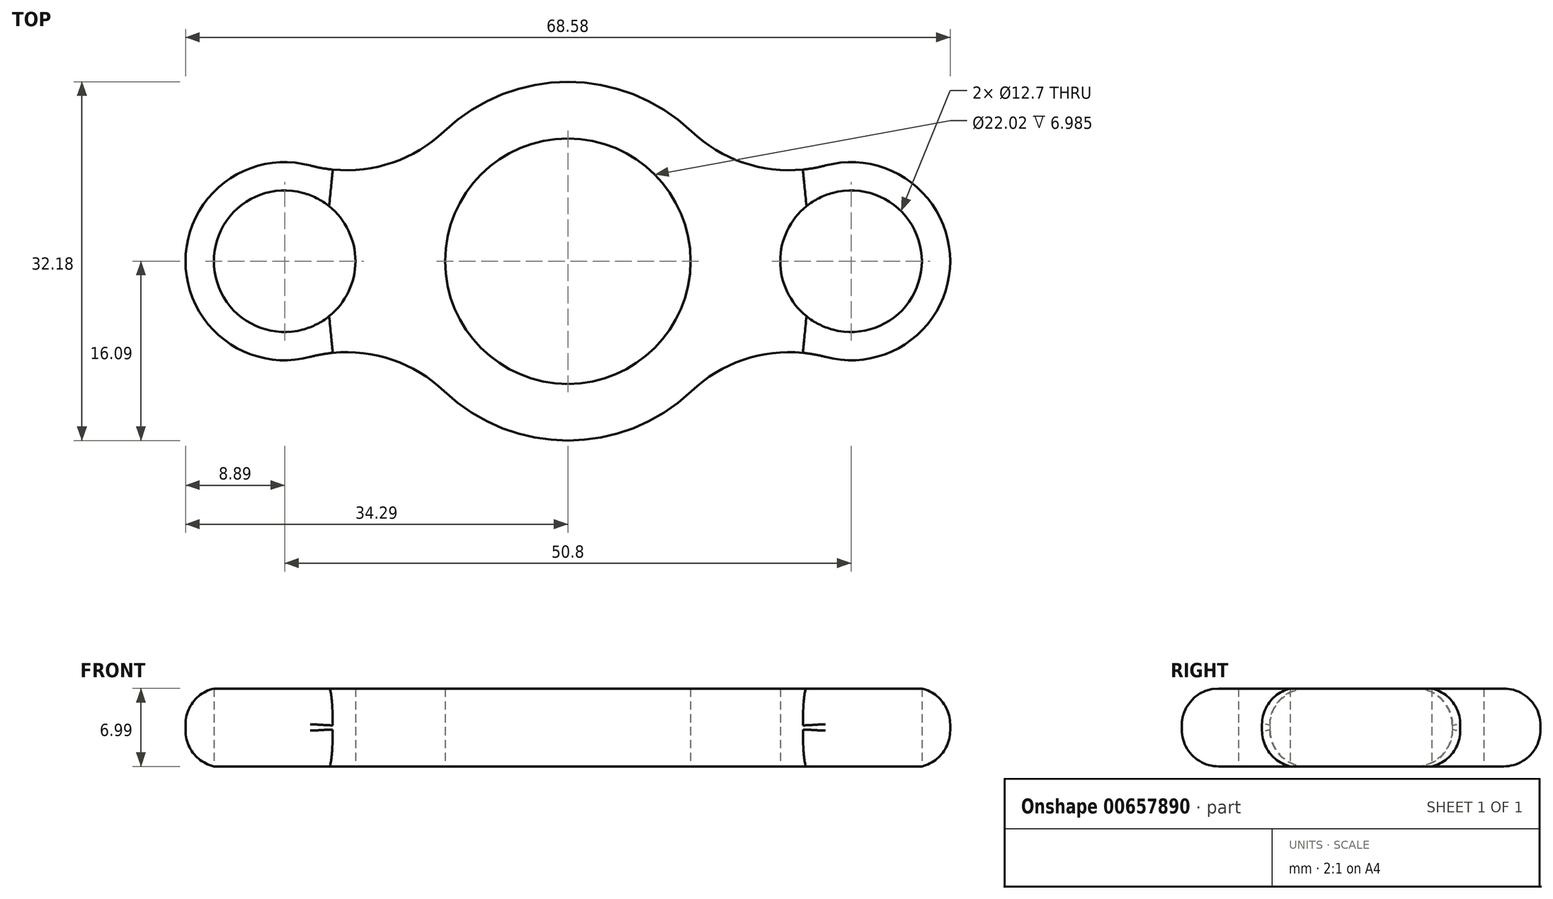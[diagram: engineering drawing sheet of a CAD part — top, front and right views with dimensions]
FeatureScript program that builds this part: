
annotation { "Feature Type Name" : "Feature", "Feature Type Description" : "" }
export const myFeature = defineFeature(function(context is Context, id is Id, definition is map)
    precondition{}
    {
        {
            var Q0;
            Q0=qCreatedBy(makeId("Top.planeOp"),FACE);
            var sketch = newSketch(context, id + "F0", { "sketchPlane" : qUnion([Q0])});
            skCircle(sketch, "E0", {"center": v(0, 0) * mm, "radius": 11.01 * mm});
            skLineSegment(sketch, "E1", {"start": v(0, 0) * mm, "end": v(25.4, 0) * mm});
            skLineSegment(sketch, "E2", {"start": v(25.4, 0) * mm, "end": v(0, 0) * mm});
            skLineSegment(sketch, "E3", {"start": v(-25.4, 0) * mm, "end": v(0, 0) * mm});
            skCircle(sketch, "E4", {"center": v(-25.4, 0) * mm, "radius": 6.35 * mm});
            skCircle(sketch, "E5", {"center": v(25.4, 0) * mm, "radius": 6.35 * mm});
            skCircle(sketch, "E6", {"center": v(0, 0) * mm, "radius": 16.1 * mm});
            skCircle(sketch, "E7", {"center": v(25.4, 0) * mm, "radius": 8.9 * mm});
            skCircle(sketch, "E8", {"center": v(-25.4, 0) * mm, "radius": 8.9 * mm});
            skArc(sketch, "E9", {"start": v(-23.11, 8.6) * mm, "mid": v(-16.7, 8.56) * mm, "end": v(-11.09, 11.66) * mm});
            skArc(sketch, "E10", {"start": v(11.09, 11.66) * mm, "mid": v(16.7, 8.56) * mm, "end": v(23.11, 8.6) * mm});
            skArc(sketch, "E11", {"start": v(-11.09, -11.66) * mm, "mid": v(-16.7, -8.56) * mm, "end": v(-23.11, -8.6) * mm});
            skArc(sketch, "E12", {"start": v(23.11, -8.6) * mm, "mid": v(16.7, -8.56) * mm, "end": v(11.09, -11.66) * mm});
            skSolve(sketch);
        }
        {
            var Q0;
            Q0 = qSketchRegion(id + "F0", true);
            extrude(context, id + "F1", {"entities" : qUnion([Q0]), "depth" : 7 * mm, "offsetDistance" : 25.4 * mm});
        }
        {
            var Q0;
            Q0=makeQuery(id+"F1.opExtrude","CAP_EDGE",EDGE,{"disambiguationData":[OSD([sQuery(id+"F0.wireOp",EDGE,"E9")])],"isStart":false});
            var Q1;
            Q1=makeQuery(id+"F1.opExtrude","CAP_EDGE",EDGE,{"disambiguationData":[OSD([sQuery(id+"F0.wireOp",EDGE,"E9")])],"isStart":true});
            fillet(context, id + "F2", {"entities" : qUnion([Q0, Q1]), "radius" : 3.3 * mm, "tangentPropagation" : true, "allowEdgeOverflow" : false});
        }
    });
